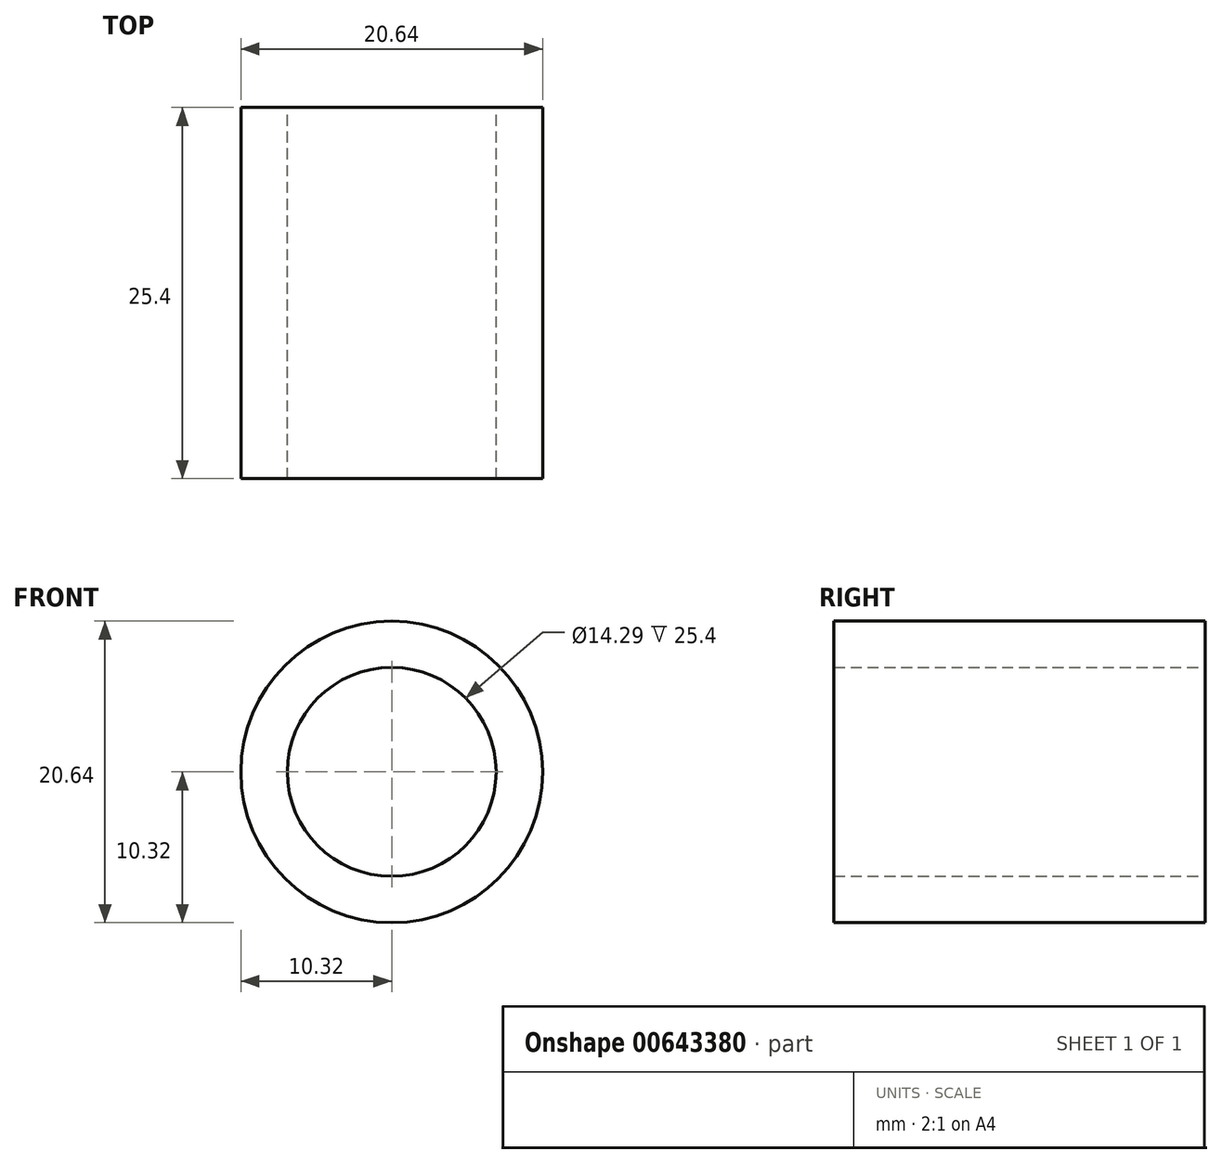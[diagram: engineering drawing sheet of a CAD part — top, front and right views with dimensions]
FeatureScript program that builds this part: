
annotation { "Feature Type Name" : "Feature", "Feature Type Description" : "" }
export const myFeature = defineFeature(function(context is Context, id is Id, definition is map)
    precondition{}
    {
        {
            var Q0;
            Q0=qCreatedBy(makeId("Front.planeOp"),FACE);
            var sketch = newSketch(context, id + "F0", { "sketchPlane" : qUnion([Q0])});
            skCircle(sketch, "E0", {"center": v(0, 0) * mm, "radius": 7.14 * mm});
            skCircle(sketch, "E1", {"center": v(0, 0) * mm, "radius": 10.32 * mm});
            skSolve(sketch);
        }
        {
            var Q0;
            Q0 = qSketchRegion(id + "F0", true);
            extrude(context, id + "F1", {"entities" : qUnion([Q0]), "depth" : 25.4 * mm, "offsetDistance" : 25.4 * mm});
        }
    });
